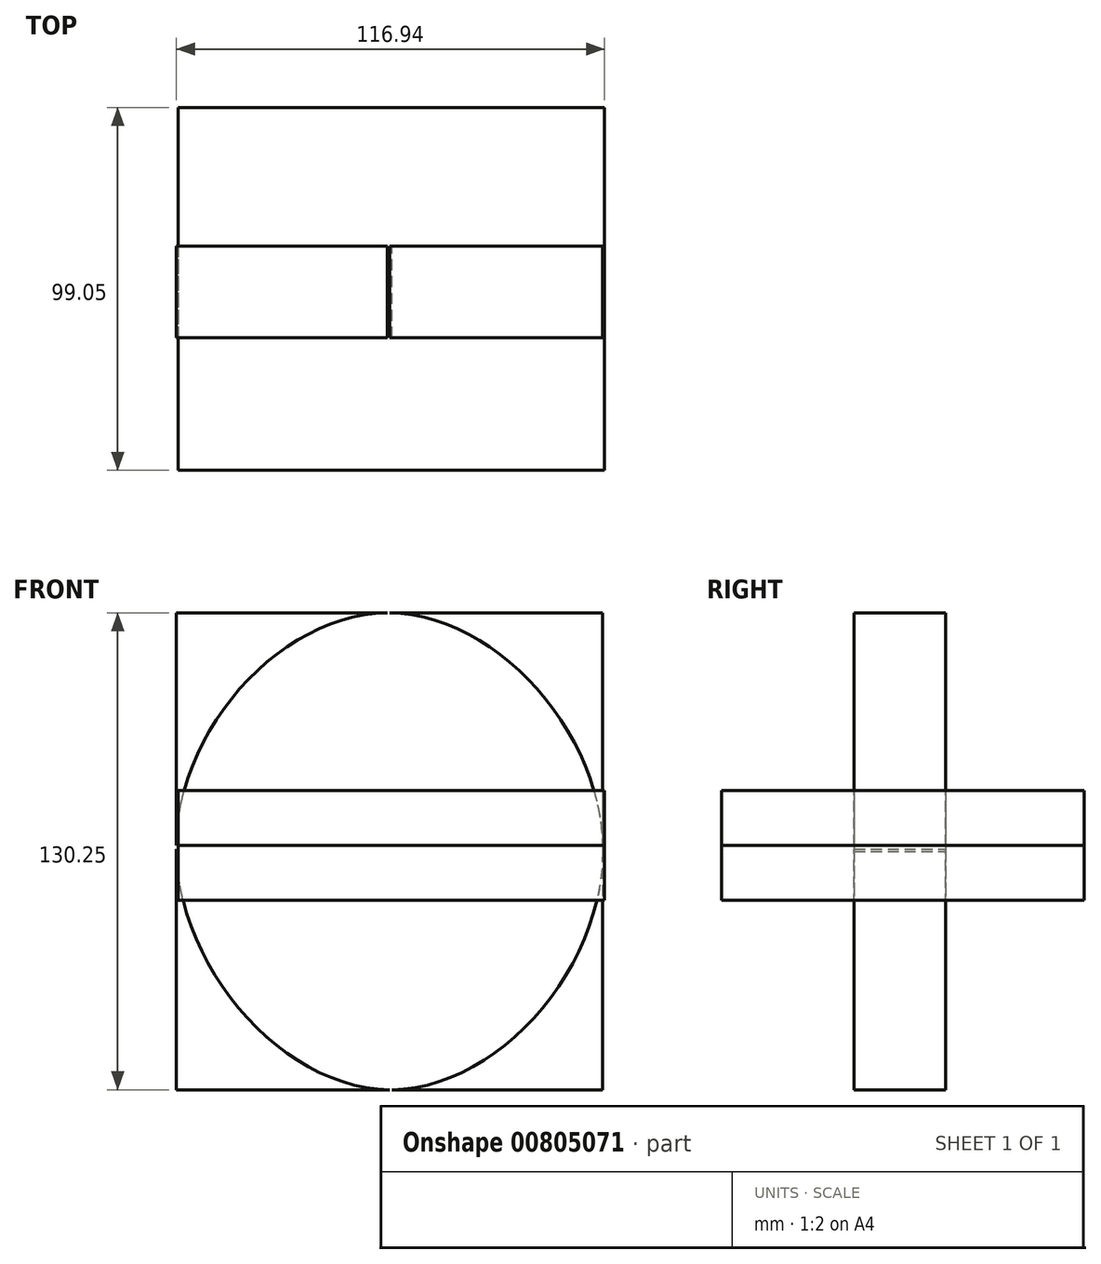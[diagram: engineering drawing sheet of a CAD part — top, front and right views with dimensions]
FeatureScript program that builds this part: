
annotation { "Feature Type Name" : "Feature", "Feature Type Description" : "" }
export const myFeature = defineFeature(function(context is Context, id is Id, definition is map)
    precondition{}
    {
        {
            var Q0;
            Q0=qCreatedBy(makeId("Front.planeOp"),FACE);
            var sketch = newSketch(context, id + "F0", { "sketchPlane" : qUnion([Q0])});
            skLineSegment(sketch, "E0.bottom", {"start": v(-58.47, 63.52) * mm, "end": v(58.01, 63.52) * mm});
            skLineSegment(sketch, "E0.top", {"start": v(-58.47, -66.73) * mm, "end": v(58.01, -66.73) * mm});
            skLineSegment(sketch, "E0.left", {"start": v(-58.47, 63.52) * mm, "end": v(-58.47, -66.73) * mm});
            skLineSegment(sketch, "E0.right", {"start": v(58.01, 63.52) * mm, "end": v(58.01, -66.73) * mm});
            skFitSpline(sketch, "E1", {"points": [v(-58.47, 0) * mm, v(-0.23, 63.52) * mm, v(58.01, -1.6) * mm, v(-0.23, -66.73) * mm, v(-58.47, 0) * mm]});
            skSolve(sketch);
        }
        {
            var Q0;
            {var subQ0=sQuery(id+"F0.wireOp",EDGE,"E0.left");var subQ1=sQuery(id+"F0.wireOp",EDGE,"E0.bottom");var subQ2=makeQuery(id+"F0.imprint","INTERSECT",VERTEX,{"derivedFrom":[subQ1,subQ0]});Q0=makeQuery(id+"F0.imprint","IMPRINT",FACE,{"disambiguationData":[TD([[makeQuery(id+"F0.imprint","IMPRINT",EDGE,{"disambiguationData":[TD([[subQ2,-1.0]])],"derivedFrom":subQ1}),-1.0]])]});}
            var Q1;
            {var subQ0=sQuery(id+"F0.wireOp",EDGE,"E0.right");var subQ1=sQuery(id+"F0.wireOp",EDGE,"E0.bottom");var subQ2=makeQuery(id+"F0.imprint","INTERSECT",VERTEX,{"derivedFrom":[subQ1,subQ0]});Q1=makeQuery(id+"F0.imprint","IMPRINT",FACE,{"disambiguationData":[TD([[makeQuery(id+"F0.imprint","IMPRINT",EDGE,{"disambiguationData":[TD([[subQ2,1.0]])],"derivedFrom":subQ1}),-1.0]])]});}
            var Q2;
            {var subQ0=sQuery(id+"F0.wireOp",EDGE,"E0.right");var subQ1=sQuery(id+"F0.wireOp",EDGE,"E0.top");var subQ2=makeQuery(id+"F0.imprint","INTERSECT",VERTEX,{"derivedFrom":[subQ1,subQ0]});Q2=makeQuery(id+"F0.imprint","IMPRINT",FACE,{"disambiguationData":[TD([[makeQuery(id+"F0.imprint","IMPRINT",EDGE,{"disambiguationData":[TD([[subQ2,1.0]])],"derivedFrom":subQ1}),1.0]])]});}
            var Q3;
            {var subQ0=sQuery(id+"F0.wireOp",EDGE,"E0.left");var subQ1=sQuery(id+"F0.wireOp",EDGE,"E0.top");var subQ2=makeQuery(id+"F0.imprint","INTERSECT",VERTEX,{"derivedFrom":[subQ1,subQ0]});Q3=makeQuery(id+"F0.imprint","IMPRINT",FACE,{"disambiguationData":[TD([[makeQuery(id+"F0.imprint","IMPRINT",EDGE,{"disambiguationData":[TD([[subQ2,-1.0]])],"derivedFrom":subQ1}),1.0]])]});}
            extrude(context, id + "F1", {"entities" : qUnion([Q0, Q1, Q2, Q3]), "depth" : 25 * mm, "offsetDistance" : 25 * mm});
        }
        {
            var Q0;
            Q0=qCreatedBy(makeId("Top.planeOp"),FACE);
            var sketch = newSketch(context, id + "F2", { "sketchPlane" : qUnion([Q0])});
            skLineSegment(sketch, "E2.bottom", {"start": v(-58.01, 37.83) * mm, "end": v(58.47, 37.83) * mm});
            skLineSegment(sketch, "E2.top", {"start": v(-58.01, -61.22) * mm, "end": v(58.47, -61.22) * mm});
            skLineSegment(sketch, "E2.left", {"start": v(-58.01, 37.83) * mm, "end": v(-58.01, -61.22) * mm});
            skLineSegment(sketch, "E2.right", {"start": v(58.47, 37.83) * mm, "end": v(58.47, -61.22) * mm});
            skSolve(sketch);
        }
        {
            var Q0;
            Q0 = qSketchRegion(id + "F2", true);
            extrude(context, id + "F3", {"entities" : qUnion([Q0]), "depth" : 15 * mm, "offsetDistance" : 25 * mm});
        }
        {
            var Q0;
            Q0=makeQuery(id+"F3.opExtrude","CAP_FACE",FACE,{"disambiguationData":[OSD([sQuery(id+"F2.wireOp",EDGE,"E2.bottom"),sQuery(id+"F2.wireOp",EDGE,"E2.top"),sQuery(id+"F2.wireOp",EDGE,"E2.left"),sQuery(id+"F2.wireOp",EDGE,"E2.right")])],"isStart":true});
            extrude(context, id + "F4", {"entities" : qUnion([Q0]), "depth" : 15 * mm, "offsetDistance" : 25 * mm});
        }
    });
